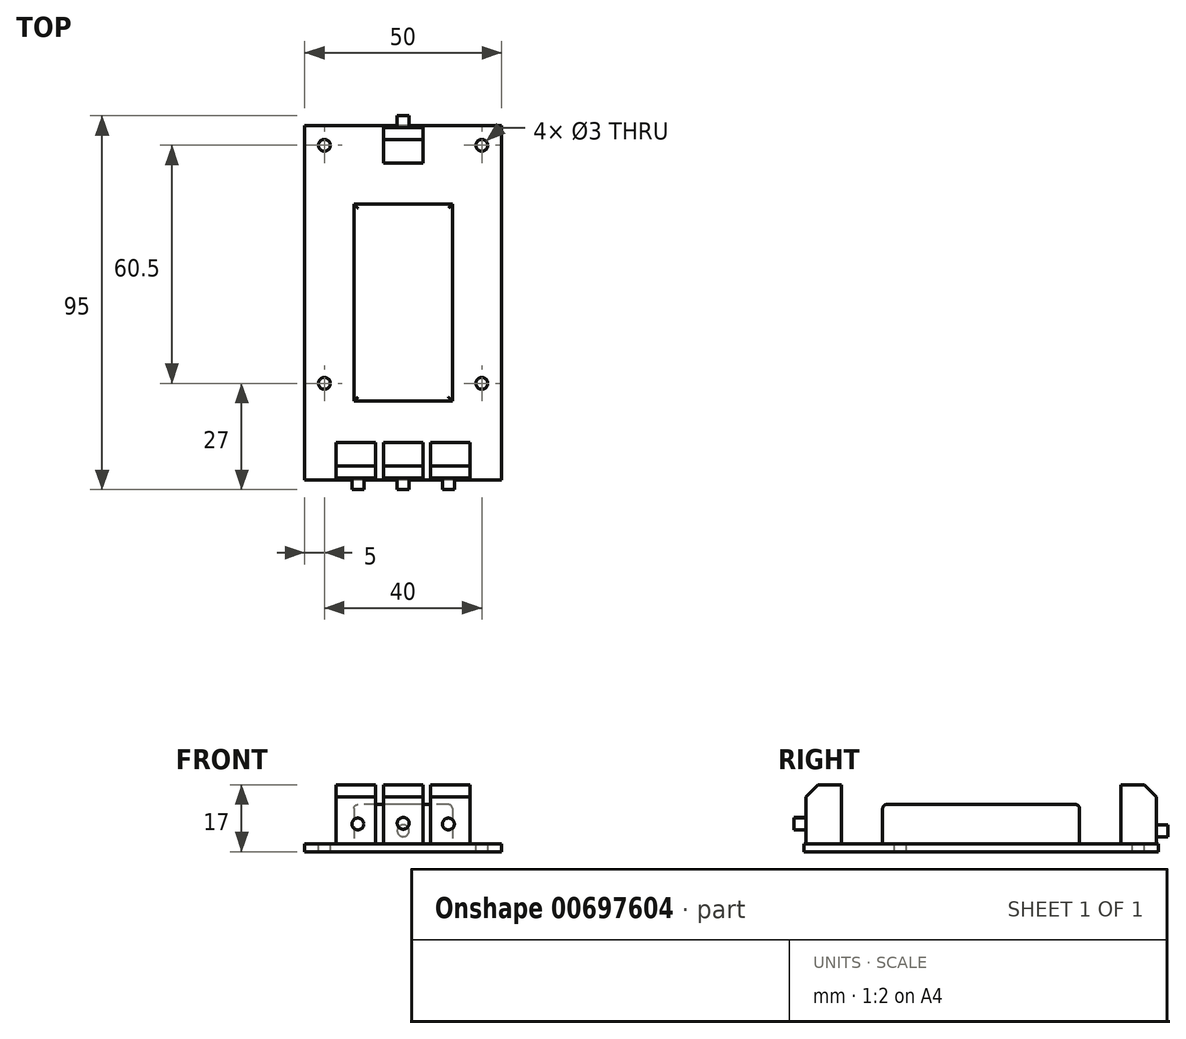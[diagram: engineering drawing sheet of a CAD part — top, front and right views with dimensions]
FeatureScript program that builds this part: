
annotation { "Feature Type Name" : "Feature", "Feature Type Description" : "" }
export const myFeature = defineFeature(function(context is Context, id is Id, definition is map)
    precondition{}
    {
        {
            var Q0;
            Q0=qCreatedBy(makeId("Top.planeOp"),FACE);
            var sketch = newSketch(context, id + "F0", { "sketchPlane" : qUnion([Q0])});
            skLineSegment(sketch, "E0.bottom", {"start": v(25, -45) * mm, "end": v(-25, -45) * mm});
            skLineSegment(sketch, "E0.top", {"start": v(25, 45) * mm, "end": v(-25, 45) * mm});
            skLineSegment(sketch, "E0.left", {"start": v(25, -45) * mm, "end": v(25, 45) * mm});
            skLineSegment(sketch, "E0.right", {"start": v(-25, -45) * mm, "end": v(-25, 45) * mm});
            skPoint(sketch, "E0.middle", {"position": v(0, 0) * mm});
            skSolve(sketch);
        }
        {
            var Q0;
            Q0 = qSketchRegion(id + "F0", true);
            extrude(context, id + "F1", {"entities" : qUnion([Q0]), "depth" : 2 * mm, "offsetDistance" : 25 * mm});
        }
        {
            var Q0;
            Q0=makeQuery(id+"F1.opExtrude","CAP_FACE",FACE,{"disambiguationData":[OSD([sQuery(id+"F0.wireOp",EDGE,"E0.bottom"),sQuery(id+"F0.wireOp",EDGE,"E0.top"),sQuery(id+"F0.wireOp",EDGE,"E0.left"),sQuery(id+"F0.wireOp",EDGE,"E0.right")])],"isStart":false});
            var sketch = newSketch(context, id + "F2", { "sketchPlane" : qUnion([Q0])});
            skCircle(sketch, "E1", {"center": v(-20, 40) * mm, "radius": 1.5 * mm});
            skCircle(sketch, "E2.MirrorC", {"center": v(20, 40) * mm, "radius": 1.5 * mm});
            skLineSegment(sketch, "E3", {"start": v(-11.18, 9.75) * mm, "end": v(11.92, 9.75) * mm});
            skCircle(sketch, "E4.MirrorC", {"center": v(-20, -20.5) * mm, "radius": 1.5 * mm});
            skCircle(sketch, "E5.MirrorC", {"center": v(20, -20.5) * mm, "radius": 1.5 * mm});
            skSolve(sketch);
        }
        {
            var Q0;
            Q0 = qSketchRegion(id + "F2", true);
            var Q1;
            Q1=makeQuery(id+"F1.opExtrude","CAP_FACE",FACE,{"disambiguationData":[OSD([sQuery(id+"F0.wireOp",EDGE,"E0.bottom"),sQuery(id+"F0.wireOp",EDGE,"E0.top"),sQuery(id+"F0.wireOp",EDGE,"E0.left"),sQuery(id+"F0.wireOp",EDGE,"E0.right")])],"isStart":true});
            extrude(context, id + "F3", {"entities" : qUnion([Q0]), "operationType" : NewBodyOperationType.REMOVE, "endBound" : BoundingType.UP_TO_SURFACE, "oppositeDirection" : true, "depth" : 25 * mm, "endBoundEntityFace" : qUnion([Q1]), "offsetDistance" : 25 * mm});
        }
        {
            var Q0;
            Q0=makeQuery(id+"F1.opExtrude","CAP_FACE",FACE,{"disambiguationData":[OSD([sQuery(id+"F0.wireOp",EDGE,"E0.bottom"),sQuery(id+"F0.wireOp",EDGE,"E0.top"),sQuery(id+"F0.wireOp",EDGE,"E0.left"),sQuery(id+"F0.wireOp",EDGE,"E0.right")])],"isStart":false});
            var sketch = newSketch(context, id + "F4", { "sketchPlane" : qUnion([Q0])});
            skLineSegment(sketch, "E6.bottom", {"start": v(12.5, -25) * mm, "end": v(-12.5, -25) * mm});
            skLineSegment(sketch, "E6.top", {"start": v(12.5, 25) * mm, "end": v(-12.5, 25) * mm});
            skLineSegment(sketch, "E6.left", {"start": v(12.5, -25) * mm, "end": v(12.5, 25) * mm});
            skLineSegment(sketch, "E6.right", {"start": v(-12.5, -25) * mm, "end": v(-12.5, 25) * mm});
            skPoint(sketch, "E6.middle", {"position": v(0, 0) * mm});
            skSolve(sketch);
        }
        {
            var Q0;
            Q0 = qSketchRegion(id + "F4", true);
            extrude(context, id + "F5", {"entities" : qUnion([Q0]), "operationType" : NewBodyOperationType.ADD, "depth" : 10 * mm, "offsetDistance" : 25 * mm});
        }
        {
            var Q0;
            Q0=makeQuery(id+"F1.opExtrude","CAP_FACE",FACE,{"disambiguationData":[OSD([sQuery(id+"F0.wireOp",EDGE,"E0.bottom"),sQuery(id+"F0.wireOp",EDGE,"E0.top"),sQuery(id+"F0.wireOp",EDGE,"E0.left"),sQuery(id+"F0.wireOp",EDGE,"E0.right")])],"isStart":false});
            var sketch = newSketch(context, id + "F6", { "sketchPlane" : qUnion([Q0])});
            skLineSegment(sketch, "E7.bottom", {"start": v(5, -44.5) * mm, "end": v(-5, -44.5) * mm});
            skLineSegment(sketch, "E7.top", {"start": v(5, -35.5) * mm, "end": v(-5, -35.5) * mm});
            skLineSegment(sketch, "E7.left", {"start": v(5, -44.5) * mm, "end": v(5, -35.5) * mm});
            skLineSegment(sketch, "E7.right", {"start": v(-5, -44.5) * mm, "end": v(-5, -35.5) * mm});
            skPoint(sketch, "E7.middle", {"position": v(0, -40) * mm});
            skLineSegment(sketch, "E8.MirrorCS", {"start": v(5, 35.5) * mm, "end": v(-5, 35.5) * mm});
            skLineSegment(sketch, "E9.MirrorCS", {"start": v(-5, 44.5) * mm, "end": v(-5, 35.5) * mm});
            skLineSegment(sketch, "E10.MirrorCS", {"start": v(5, 44.5) * mm, "end": v(5, 35.5) * mm});
            skLineSegment(sketch, "E11.MirrorCS", {"start": v(5, 44.5) * mm, "end": v(-5, 44.5) * mm});
            skLineSegment(sketch, "E12", {"start": v(6, -45) * mm, "end": v(6, -32.88) * mm});
            skLineSegment(sketch, "E13.MirrorCS", {"start": v(7, -44.5) * mm, "end": v(7, -35.5) * mm});
            skLineSegment(sketch, "E14.MirrorCS", {"start": v(7, -35.5) * mm, "end": v(17, -35.5) * mm});
            skLineSegment(sketch, "E15.MirrorCS", {"start": v(17, -44.5) * mm, "end": v(17, -35.5) * mm});
            skLineSegment(sketch, "E16.MirrorCS", {"start": v(7, -44.5) * mm, "end": v(17, -44.5) * mm});
            skLineSegment(sketch, "E17.MirrorCS", {"start": v(-7, -35.5) * mm, "end": v(-17, -35.5) * mm});
            skLineSegment(sketch, "E18.MirrorCS", {"start": v(-7, -44.5) * mm, "end": v(-7, -35.5) * mm});
            skLineSegment(sketch, "E19.MirrorCS", {"start": v(-7, -44.5) * mm, "end": v(-17, -44.5) * mm});
            skLineSegment(sketch, "E20.MirrorCS", {"start": v(-17, -44.5) * mm, "end": v(-17, -35.5) * mm});
            skSolve(sketch);
        }
        {
            var Q0;
            Q0 = qSketchRegion(id + "F6", true);
            extrude(context, id + "F7", {"entities" : qUnion([Q0]), "operationType" : NewBodyOperationType.ADD, "depth" : 15 * mm, "offsetDistance" : 25 * mm});
        }
        {
            var Q0;
            Q0=makeQuery(id+"F7.opExtrude","SWEPT_FACE",FACE,{"disambiguationData":[OSD([sQuery(id+"F6.wireOp",EDGE,"E11.MirrorCS")])]});
            var sketch = newSketch(context, id + "F8", { "sketchPlane" : qUnion([Q0])});
            skCircle(sketch, "E21", {"center": v(0, 5.33) * mm, "radius": 1.5 * mm});
            skSolve(sketch);
        }
        {
            var Q0;
            Q0 = qSketchRegion(id + "F8", true);
            extrude(context, id + "F9", {"entities" : qUnion([Q0]), "operationType" : NewBodyOperationType.ADD, "depth" : 3 * mm, "offsetDistance" : 25 * mm});
        }
        {
            var Q0;
            Q0=makeQuery(id+"F7.opExtrude","SWEPT_FACE",FACE,{"disambiguationData":[OSD([sQuery(id+"F6.wireOp",EDGE,"E7.bottom")])]});
            var sketch = newSketch(context, id + "F10", { "sketchPlane" : qUnion([Q0])});
            skCircle(sketch, "E22", {"center": v(0, 7.22) * mm, "radius": 1.5 * mm});
            skCircle(sketch, "E23", {"center": v(-11.5, 7.05) * mm, "radius": 1.5 * mm});
            skCircle(sketch, "E24.MirrorC", {"center": v(11.5, 7.05) * mm, "radius": 1.5 * mm});
            skSolve(sketch);
        }
        {
            var Q0;
            Q0 = qSketchRegion(id + "F10", true);
            extrude(context, id + "F11", {"entities" : qUnion([Q0]), "operationType" : NewBodyOperationType.ADD, "depth" : 3 * mm, "offsetDistance" : 25 * mm});
        }
        {
            var Q0;
            Q0=makeQuery(id+"F5.opExtrude","CAP_FACE",FACE,{"disambiguationData":[OSD([sQuery(id+"F4.wireOp",EDGE,"E6.bottom"),sQuery(id+"F4.wireOp",EDGE,"E6.top"),sQuery(id+"F4.wireOp",EDGE,"E6.left"),sQuery(id+"F4.wireOp",EDGE,"E6.right")])],"isStart":false});
            fillet(context, id + "F12", {"entities" : qUnion([Q0]), "radius" : 1 * mm, "tangentPropagation" : true, "allowEdgeOverflow" : false});
        }
        {
            var Q0;
            Q0=makeQuery(id+"F7.opExtrude","CAP_EDGE",EDGE,{"disambiguationData":[OSD([sQuery(id+"F6.wireOp",EDGE,"E19.MirrorCS")])],"isStart":false});
            var Q1;
            Q1=makeQuery(id+"F7.opExtrude","CAP_EDGE",EDGE,{"disambiguationData":[OSD([sQuery(id+"F6.wireOp",EDGE,"E7.bottom")])],"isStart":false});
            var Q2;
            Q2=makeQuery(id+"F7.opExtrude","CAP_EDGE",EDGE,{"disambiguationData":[OSD([sQuery(id+"F6.wireOp",EDGE,"E16.MirrorCS")])],"isStart":false});
            var Q3;
            Q3=makeQuery(id+"F7.opExtrude","CAP_EDGE",EDGE,{"disambiguationData":[OSD([sQuery(id+"F6.wireOp",EDGE,"E11.MirrorCS")])],"isStart":false});
            chamfer(context, id + "F13", {"entities" : qUnion([Q0, Q1, Q2, Q3]), "width" : 3 * mm, "tangentPropagation" : true});
        }
    });
